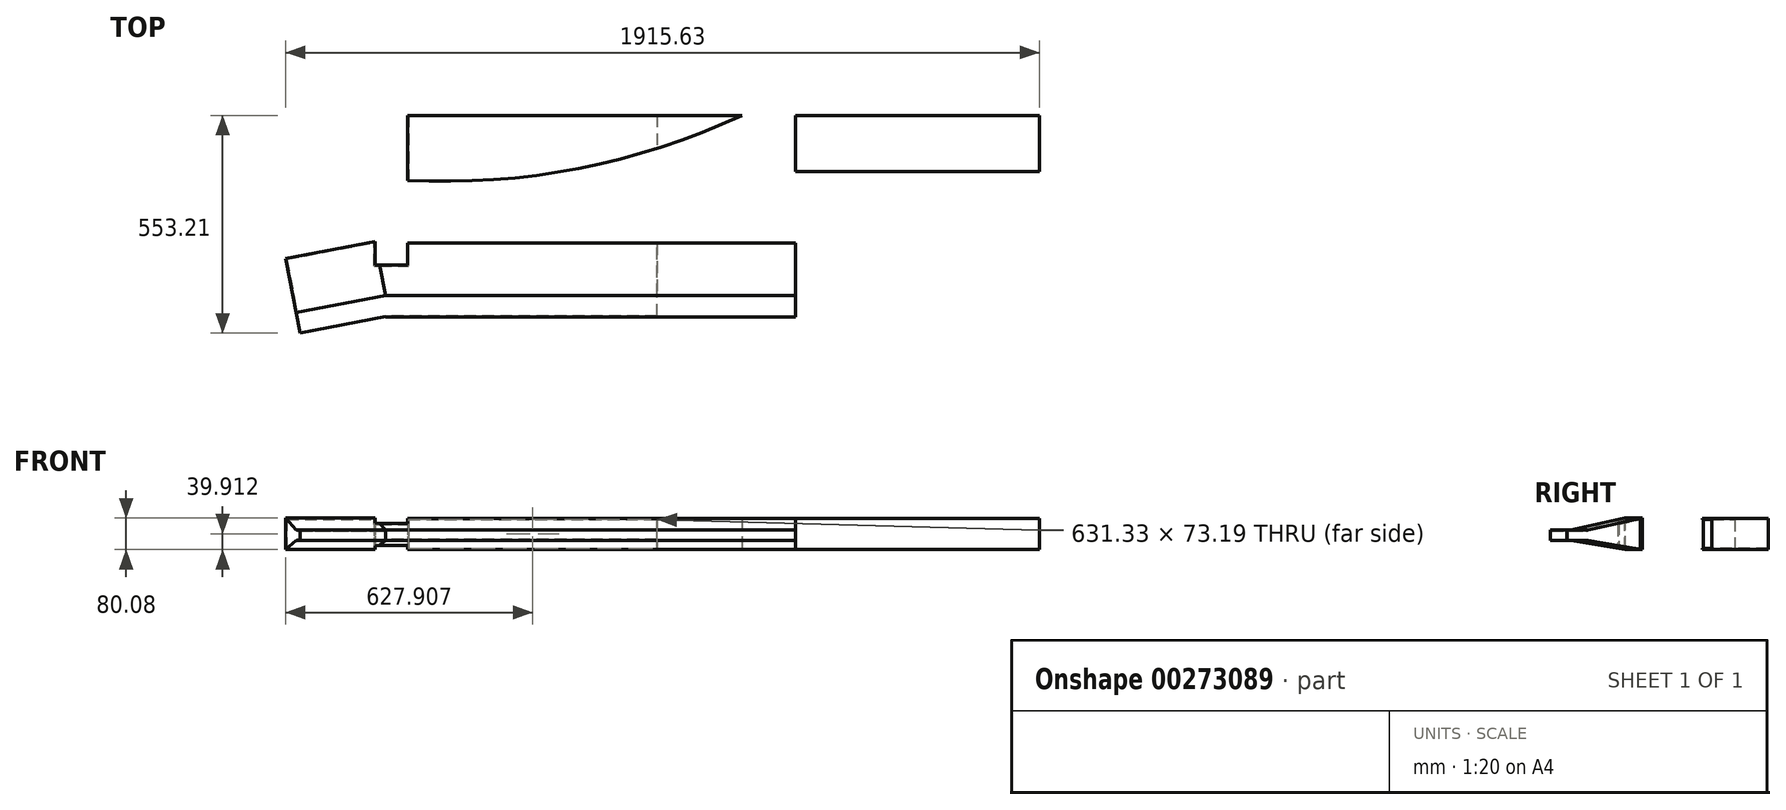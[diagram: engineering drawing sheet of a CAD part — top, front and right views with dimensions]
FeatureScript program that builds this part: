
annotation { "Feature Type Name" : "Feature", "Feature Type Description" : "" }
export const myFeature = defineFeature(function(context is Context, id is Id, definition is map)
    precondition{}
    {
        {
            var Q0;
            Q0=qCreatedBy(makeId("Front.planeOp"),FACE);
            var sketch = newSketch(context, id + "F0", { "sketchPlane" : qUnion([Q0])});
            skLineSegment(sketch, "E0.bottom", {"start": v(42.11, 43.57) * mm, "end": v(-40.25, 43.57) * mm});
            skLineSegment(sketch, "E0.top", {"start": v(42.11, -36.51) * mm, "end": v(-40.25, -36.51) * mm});
            skLineSegment(sketch, "E0.left", {"start": v(42.11, 43.57) * mm, "end": v(42.11, -36.51) * mm});
            skLineSegment(sketch, "E0.right", {"start": v(-40.25, 43.57) * mm, "end": v(-40.25, -36.51) * mm});
            skSolve(sketch);
        }
        {
            var Q0;
            Q0 = qSketchRegion(id + "F0", true);
            extrude(context, id + "F1", {"entities" : qUnion([Q0]), "depth" : 25.4 * mm});
        }
        {
            var Q0;
            Q0=makeQuery(id+"F1.opExtrude","CAP_FACE",FACE,{"disambiguationData":[OSD([sQuery(id+"F0.wireOp",EDGE,"E0.bottom"),sQuery(id+"F0.wireOp",EDGE,"E0.top"),sQuery(id+"F0.wireOp",EDGE,"E0.left"),sQuery(id+"F0.wireOp",EDGE,"E0.right")])],"isStart":false});
            var sketch = newSketch(context, id + "F2", { "sketchPlane" : qUnion([Q0])});
            skLineSegment(sketch, "E1.bottom", {"start": v(13.9, -13.28) * mm, "end": v(-13.9, -13.28) * mm});
            skLineSegment(sketch, "E1.top", {"start": v(13.9, 13.28) * mm, "end": v(-13.9, 13.28) * mm});
            skLineSegment(sketch, "E1.left", {"start": v(13.9, -13.28) * mm, "end": v(13.9, 13.28) * mm});
            skLineSegment(sketch, "E1.right", {"start": v(-13.9, -13.28) * mm, "end": v(-13.9, 13.28) * mm});
            skPoint(sketch, "E1.middle", {"position": v(0, 0) * mm});
            skSolve(sketch);
        }
        {
            var Q0;
            Q0=makeQuery(id+"F2.imprint","IMPRINT",FACE,{"disambiguationData":[TD([[makeQuery(id+"F2.imprint","IMPRINT",EDGE,{"derivedFrom":sQuery(id+"F2.wireOp",EDGE,"E1.bottom")}),-1.0]])]});
            extrude(context, id + "F3", {"entities" : qUnion([Q0]), "operationType" : NewBodyOperationType.ADD, "depth" : 187.42 * mm});
        }
        {
            var Q0;
            Q0=makeQuery(id+"F3.opExtrude","SWEPT_FACE",FACE,{"disambiguationData":[OSD([sQuery(id+"F2.wireOp",EDGE,"E1.left")])]});
            extrude(context, id + "F4", {"entities" : qUnion([Q0]), "operationType" : NewBodyOperationType.ADD, "depth" : 25.4 * mm});
        }
        {
            var Q0;
            Q0=makeQuery(id+"F4.opExtrude","CAP_FACE",FACE,{"disambiguationData":[OSD([sQuery(id+"F2.wireOp",EDGE,"E1.left")])],"isStart":false});
            var sketch = newSketch(context, id + "F5", { "sketchPlane" : qUnion([Q0])});
            skLineSegment(sketch, "E2.bottom", {"start": v(-158.98, 64.6) * mm, "end": v(-21, 64.6) * mm});
            skLineSegment(sketch, "E2.top", {"start": v(-158.98, -64.89) * mm, "end": v(-21, -64.89) * mm});
            skLineSegment(sketch, "E2.left", {"start": v(-158.98, 64.6) * mm, "end": v(-158.98, -64.89) * mm});
            skLineSegment(sketch, "E2.right", {"start": v(-21, 64.6) * mm, "end": v(-21, -64.89) * mm});
            skSolve(sketch);
        }
        {
            var Q0;
            Q0 = qSketchRegion(id + "F5", true);
            extrude(context, id + "F6", {"entities" : qUnion([Q0]), "operationType" : NewBodyOperationType.REMOVE, "oppositeDirection" : true, "depth" : 111.05 * mm});
        }
        {
            var Q0;
            Q0=makeQuery(id+"F6.boolean.opBoolean","COPY",FACE,{"derivedFrom":makeQuery(id+"F6.opExtrude","SWEPT_FACE",FACE,{"disambiguationData":[OSD([sQuery(id+"F5.wireOp",EDGE,"E2.right")])]})});
            var Q1;
            Q1=makeQuery(id+"F6.boolean.opBoolean","COPY",FACE,{"derivedFrom":makeQuery(id+"F6.opExtrude","SWEPT_FACE",FACE,{"disambiguationData":[OSD([sQuery(id+"F5.wireOp",EDGE,"E2.left")])]})});
            loft(context, id + "F7", {"operationType" : NewBodyOperationType.ADD, "sheetProfilesArray" : [{ "sheetProfileEntities" : qUnion([Q0]) }, { "sheetProfileEntities" : qUnion([Q1]) }]});
        }
        {
            var Q0;
            Q0=makeQuery(id+"F7.opLoft","SWEPT_FACE",FACE,{"disambiguationData":[OSD([sQuery(id+"F0.wireOp",EDGE,"E0.bottom"),sQuery(id+"F0.wireOp",EDGE,"E0.top"),sQuery(id+"F0.wireOp",EDGE,"E0.right"),sQuery(id+"F2.wireOp",EDGE,"E1.bottom"),sQuery(id+"F2.wireOp",EDGE,"E1.top"),sQuery(id+"F2.wireOp",EDGE,"E1.left"),sQuery(id+"F2.wireOp",EDGE,"E1.right"),sQuery(id+"F5.wireOp",EDGE,"E2.left"),sQuery(id+"F5.wireOp",EDGE,"E2.right")])]});
            extrude(context, id + "F8", {"entities" : qUnion([Q0]), "operationType" : NewBodyOperationType.ADD, "depth" : 231.45 * mm});
        }
        {
            var Q0;
            {var subQ0=sQuery(id+"F2.wireOp",EDGE,"E1.left");Q0=makeQuery(id+"F7.boolean.opBoolean","MERGE",FACE,{"derivedFrom":[makeQuery(id+"F4.opExtrude","CAP_FACE",FACE,{"disambiguationData":[OSD([subQ0])],"isStart":false}),makeQuery(id+"F7.opLoft","SWEPT_FACE",FACE,{"disambiguationData":[OSD([sQuery(id+"F0.wireOp",EDGE,"E0.bottom"),sQuery(id+"F0.wireOp",EDGE,"E0.top"),sQuery(id+"F2.wireOp",EDGE,"E1.bottom"),sQuery(id+"F2.wireOp",EDGE,"E1.top"),subQ0,sQuery(id+"F5.wireOp",EDGE,"E2.bottom"),sQuery(id+"F5.wireOp",EDGE,"E2.top"),sQuery(id+"F5.wireOp",EDGE,"E2.left"),sQuery(id+"F5.wireOp",EDGE,"E2.right")])]})]});}
            extrude(context, id + "F9", {"entities" : qUnion([Q0]), "operationType" : NewBodyOperationType.ADD, "depth" : 639.22 * mm});
        }
        {
            var Q0;
            Q0=makeQuery(id+"F8.opExtrude","SWEPT_FACE",FACE,{"disambiguationData":[OSD([sQuery(id+"F2.wireOp",EDGE,"E1.bottom"),sQuery(id+"F2.wireOp",EDGE,"E1.top"),sQuery(id+"F2.wireOp",EDGE,"E1.left"),sQuery(id+"F2.wireOp",EDGE,"E1.right"),sQuery(id+"F5.wireOp",EDGE,"E2.left")])]});
            extrude(context, id + "F10", {"entities" : qUnion([Q0]), "operationType" : NewBodyOperationType.ADD, "depth" : 52.64 * mm});
        }
        {
            var Q0;
            Q0=makeQuery(id+"F1.opExtrude","CAP_FACE",FACE,{"disambiguationData":[OSD([sQuery(id+"F0.wireOp",EDGE,"E0.bottom"),sQuery(id+"F0.wireOp",EDGE,"E0.top"),sQuery(id+"F0.wireOp",EDGE,"E0.left"),sQuery(id+"F0.wireOp",EDGE,"E0.right")])],"isStart":true});
            extrude(context, id + "F11", {"entities" : qUnion([Q0]), "operationType" : NewBodyOperationType.REMOVE, "oppositeDirection" : true, "depth" : 80.62 * mm});
        }
        {
            var Q0;
            Q0=makeQuery(id+"F9.opExtrude","SWEPT_FACE",FACE,{"disambiguationData":[OSD([sQuery(id+"F0.wireOp",EDGE,"E0.bottom"),sQuery(id+"F0.wireOp",EDGE,"E0.top"),sQuery(id+"F0.wireOp",EDGE,"E0.left"),sQuery(id+"F0.wireOp",EDGE,"E0.right"),sQuery(id+"F5.wireOp",EDGE,"E2.bottom"),sQuery(id+"F5.wireOp",EDGE,"E2.top"),sQuery(id+"F5.wireOp",EDGE,"E2.left"),sQuery(id+"F5.wireOp",EDGE,"E2.right")])]});
            shell(context, id + "F12", {"entities" : qUnion([Q0]), "thickness" : 2.54 * mm});
        }
        {
            var Q0;
            Q0=makeQuery(id+"F9.opExtrude","CAP_FACE",FACE,{"disambiguationData":[OSD([sQuery(id+"F0.wireOp",EDGE,"E0.bottom"),sQuery(id+"F0.wireOp",EDGE,"E0.top"),sQuery(id+"F2.wireOp",EDGE,"E1.bottom"),sQuery(id+"F2.wireOp",EDGE,"E1.top"),sQuery(id+"F2.wireOp",EDGE,"E1.left"),sQuery(id+"F5.wireOp",EDGE,"E2.bottom"),sQuery(id+"F5.wireOp",EDGE,"E2.top"),sQuery(id+"F5.wireOp",EDGE,"E2.left"),sQuery(id+"F5.wireOp",EDGE,"E2.right")])],"isStart":false});
            extrude(context, id + "F13", {"entities" : qUnion([Q0]), "operationType" : NewBodyOperationType.ADD, "depth" : 349.02 * mm});
        }
        {
            var Q0;
            {var subQ0=sQuery(id+"F5.wireOp",EDGE,"E2.right");var subQ1=sQuery(id+"F5.wireOp",EDGE,"E2.left");var subQ2=sQuery(id+"F5.wireOp",EDGE,"E2.top");var subQ3=sQuery(id+"F5.wireOp",EDGE,"E2.bottom");var subQ4=sQuery(id+"F0.wireOp",EDGE,"E0.right");var subQ5=sQuery(id+"F0.wireOp",EDGE,"E0.left");var subQ6=sQuery(id+"F0.wireOp",EDGE,"E0.top");var subQ7=sQuery(id+"F0.wireOp",EDGE,"E0.bottom");Q0=makeQuery(id+"F13.boolean.opBoolean","MERGE",FACE,{"derivedFrom":[makeQuery(id+"F9.opExtrude","SWEPT_FACE",FACE,{"disambiguationData":[OSD([subQ7,subQ6,subQ5,subQ4,subQ3,subQ2,subQ1,subQ0])]}),makeQuery(id+"F13.opExtrude","SWEPT_FACE",FACE,{"disambiguationData":[OSD([subQ7,subQ6,subQ5,subQ4,subQ3,subQ2,subQ1,subQ0])]})]});}
            extrude(context, id + "F14", {"entities" : qUnion([Q0]), "operationType" : NewBodyOperationType.ADD, "depth" : 324.52 * mm});
        }
        {
            var Q0;
            {var subQ0=sQuery(id+"F5.wireOp",EDGE,"E2.right");var subQ1=sQuery(id+"F5.wireOp",EDGE,"E2.left");var subQ2=sQuery(id+"F5.wireOp",EDGE,"E2.top");var subQ3=sQuery(id+"F5.wireOp",EDGE,"E2.bottom");var subQ4=sQuery(id+"F2.wireOp",EDGE,"E1.right");var subQ5=sQuery(id+"F2.wireOp",EDGE,"E1.left");var subQ6=sQuery(id+"F2.wireOp",EDGE,"E1.bottom");var subQ7=sQuery(id+"F0.wireOp",EDGE,"E0.right");var subQ8=sQuery(id+"F0.wireOp",EDGE,"E0.top");var subQ9=makeQuery(id+"F7.opLoft","SWEPT_FACE",FACE,{"disambiguationData":[OSD([subQ8,subQ7,subQ6,subQ5,subQ4,subQ3,subQ2,subQ1,subQ0])]});var subQ10=sQuery(id+"F2.wireOp",EDGE,"E1.top");var subQ11=sQuery(id+"F0.wireOp",EDGE,"E0.bottom");var subQ12=sQuery(id+"F0.wireOp",EDGE,"E0.left");var subQ13=makeQuery(id+"F1.opExtrude","CAP_FACE",FACE,{"disambiguationData":[OSD([subQ11,subQ8,subQ12,subQ7])],"isStart":false});var subQ14=makeQuery(id+"F7.boolean.opBoolean","TWEAK_VERTEX",VERTEX,{"derivedFrom":[makeQuery(id+"F6.boolean.opBoolean","COPY",FACE,{"derivedFrom":makeQuery(id+"F6.opExtrude","CAP_FACE",FACE,{"disambiguationData":[OSD([subQ3,subQ2,subQ1,subQ0])],"isStart":true})}),makeQuery(id+"F4.opExtrude","CAP_FACE",FACE,{"disambiguationData":[OSD([subQ5])],"isStart":false}),subQ13,makeQuery(id+"F7.opLoft","SWEPT_FACE",FACE,{"disambiguationData":[OSD([subQ11,subQ8,subQ6,subQ10,subQ5,subQ3,subQ2,subQ1,subQ0])]}),subQ9]});Q0=makeQuery(id+"F14.opExtrude","SWEPT_FACE",FACE,{"disambiguationData":[OSD([subQ11,subQ8,subQ12,subQ7,subQ6,subQ10,subQ5,subQ4,subQ3,subQ2,subQ1,subQ0]),TDD([makeQuery(id+"F13.boolean.opBoolean","MERGE",EDGE,{"derivedFrom":[makeQuery(id+"F9.boolean.opBoolean","SPLIT",EDGE,{"disambiguationData":[TD([makeQuery(id+"F9.opExtrude","CAP_FACE",FACE,{"disambiguationData":[OSD([subQ11,subQ8,subQ6,subQ10,subQ5,subQ3,subQ2,subQ1,subQ0])],"isStart":false})])],"derivedFrom":makeQuery(id+"F9.opExtrude","SWEPT_EDGE",EDGE,{"disambiguationData":[OSD([subQ11,subQ8,subQ12,subQ7,subQ6,subQ10,subQ5,subQ4,subQ3,subQ2,subQ1,subQ0]),TDD([subQ14])]})}),makeQuery(id+"F13.opExtrude","SWEPT_EDGE",EDGE,{"disambiguationData":[OSD([subQ11,subQ8,subQ12,subQ7,subQ6,subQ10,subQ5,subQ4,subQ3,subQ2,subQ1,subQ0]),TDD([makeQuery(id+"F9.opExtrude","CAP_VERTEX",VERTEX,{"disambiguationData":[OSD([subQ11,subQ8,subQ12,subQ7,subQ6,subQ10,subQ5,subQ4,subQ3,subQ2,subQ1,subQ0]),TDD([subQ14])],"isStart":false})])]})]})])]});}
            var sketch = newSketch(context, id + "F15", { "sketchPlane" : qUnion([Q0])});
            skArc(sketch, "E3", {"start": v(0, -136.86) * mm, "mid": v(521.51, -173.43) * mm, "end": v(1009.83, -360.12) * mm});
            skPoint(sketch, "E3.startSnap0", {"position": v(42.11, -136.86) * mm});
            skSolve(sketch);
        }
        {
            var Q0;
            {var subQ0=sQuery(id+"F15.wireOp",EDGE,"E3");var subQ1=sQuery(id+"F5.wireOp",EDGE,"E2.right");var subQ2=sQuery(id+"F5.wireOp",EDGE,"E2.left");var subQ3=sQuery(id+"F5.wireOp",EDGE,"E2.top");var subQ4=sQuery(id+"F5.wireOp",EDGE,"E2.bottom");var subQ5=sQuery(id+"F2.wireOp",EDGE,"E1.left");var subQ6=sQuery(id+"F2.wireOp",EDGE,"E1.bottom");var subQ7=sQuery(id+"F0.wireOp",EDGE,"E0.top");var subQ8=makeQuery(id+"F9.opExtrude","SWEPT_FACE",FACE,{"disambiguationData":[OSD([subQ7,subQ6,subQ5,subQ4,subQ3,subQ2,subQ1])]});var subQ9=sQuery(id+"F0.wireOp",EDGE,"E0.right");var subQ10=sQuery(id+"F0.wireOp",EDGE,"E0.left");var subQ11=sQuery(id+"F0.wireOp",EDGE,"E0.bottom");var subQ12=makeQuery(id+"F9.opExtrude","SWEPT_FACE",FACE,{"disambiguationData":[OSD([subQ11,subQ7,subQ10,subQ9,subQ4,subQ3,subQ2,subQ1])]});var subQ13=sQuery(id+"F2.wireOp",EDGE,"E1.right");var subQ14=makeQuery(id+"F7.opLoft","SWEPT_FACE",FACE,{"disambiguationData":[OSD([subQ7,subQ9,subQ6,subQ5,subQ13,subQ4,subQ3,subQ2,subQ1])]});var subQ15=makeQuery(id+"F1.opExtrude","CAP_FACE",FACE,{"disambiguationData":[OSD([subQ11,subQ7,subQ10,subQ9])],"isStart":false});var subQ16=subQ15;var subQ17=makeQuery(id+"F1.opExtrude","SWEPT_FACE",FACE,{"disambiguationData":[OSD([subQ10])]});var subQ18=makeQuery(id+"F14.opExtrude","SWEPT_EDGE",EDGE,{"disambiguationData":[OSD([subQ11,subQ7,subQ10,subQ9,subQ6,subQ5,subQ13,subQ4,subQ3,subQ2,subQ1]),TDD([makeQuery(id+"F9.boolean.opBoolean","TWEAK_VERTEX",VERTEX,{"derivedFrom":[subQ17,subQ16,subQ14,subQ12,subQ8]})])]});var subQ19=makeQuery(id+"F15.imprint","INTERSECT",VERTEX,{"derivedFrom":[subQ18,subQ0]});Q0=makeQuery(id+"F15.imprint","IMPRINT",FACE,{"disambiguationData":[TD([[makeQuery(id+"F15.imprint","IMPRINT",EDGE,{"disambiguationData":[TD([[subQ19,-1.0]])],"derivedFrom":subQ0}),-1.0]])]});}
            extrude(context, id + "F16", {"entities" : qUnion([Q0]), "operationType" : NewBodyOperationType.REMOVE, "oppositeDirection" : true, "depth" : 839.17 * mm});
        }
        {
            var Q0;
            {var subQ0=sQuery(id+"F5.wireOp",EDGE,"E2.right");var subQ1=sQuery(id+"F5.wireOp",EDGE,"E2.left");var subQ2=sQuery(id+"F5.wireOp",EDGE,"E2.top");var subQ3=sQuery(id+"F5.wireOp",EDGE,"E2.bottom");var subQ4=sQuery(id+"F0.wireOp",EDGE,"E0.right");var subQ5=sQuery(id+"F0.wireOp",EDGE,"E0.left");var subQ6=sQuery(id+"F0.wireOp",EDGE,"E0.top");var subQ7=sQuery(id+"F0.wireOp",EDGE,"E0.bottom");Q0=makeQuery(id+"F14.boolean.opBoolean","MERGE",FACE,{"derivedFrom":[makeQuery(id+"F13.opExtrude","CAP_FACE",FACE,{"disambiguationData":[OSD([subQ7,subQ6,sQuery(id+"F2.wireOp",EDGE,"E1.bottom"),sQuery(id+"F2.wireOp",EDGE,"E1.top"),sQuery(id+"F2.wireOp",EDGE,"E1.left"),subQ3,subQ2,subQ1,subQ0])],"isStart":false}),makeQuery(id+"F14.opExtrude","SWEPT_FACE",FACE,{"disambiguationData":[OSD([subQ7,subQ6,subQ5,subQ4,subQ3,subQ2,subQ1,subQ0]),TDD([makeQuery(id+"F13.opExtrude","CAP_EDGE",EDGE,{"disambiguationData":[OSD([subQ7,subQ6,subQ5,subQ4,subQ3,subQ2,subQ1,subQ0])],"isStart":false})])]})]});}
            var sketch = newSketch(context, id + "F17", { "sketchPlane" : qUnion([Q0])});
            skLineSegment(sketch, "E4.bottom", {"start": v(156.18, 42.6) * mm, "end": v(299.12, 42.6) * mm});
            skLineSegment(sketch, "E4.top", {"start": v(156.18, -35.77) * mm, "end": v(299.12, -35.77) * mm});
            skLineSegment(sketch, "E4.left", {"start": v(156.18, 42.6) * mm, "end": v(156.18, -35.77) * mm});
            skLineSegment(sketch, "E4.right", {"start": v(299.12, 42.6) * mm, "end": v(299.12, -35.77) * mm});
            skSolve(sketch);
        }
        {
            var Q0;
            Q0 = qSketchRegion(id + "F17", true);
            extrude(context, id + "F18", {"entities" : qUnion([Q0]), "operationType" : NewBodyOperationType.ADD, "depth" : 620.5 * mm});
        }
    });
